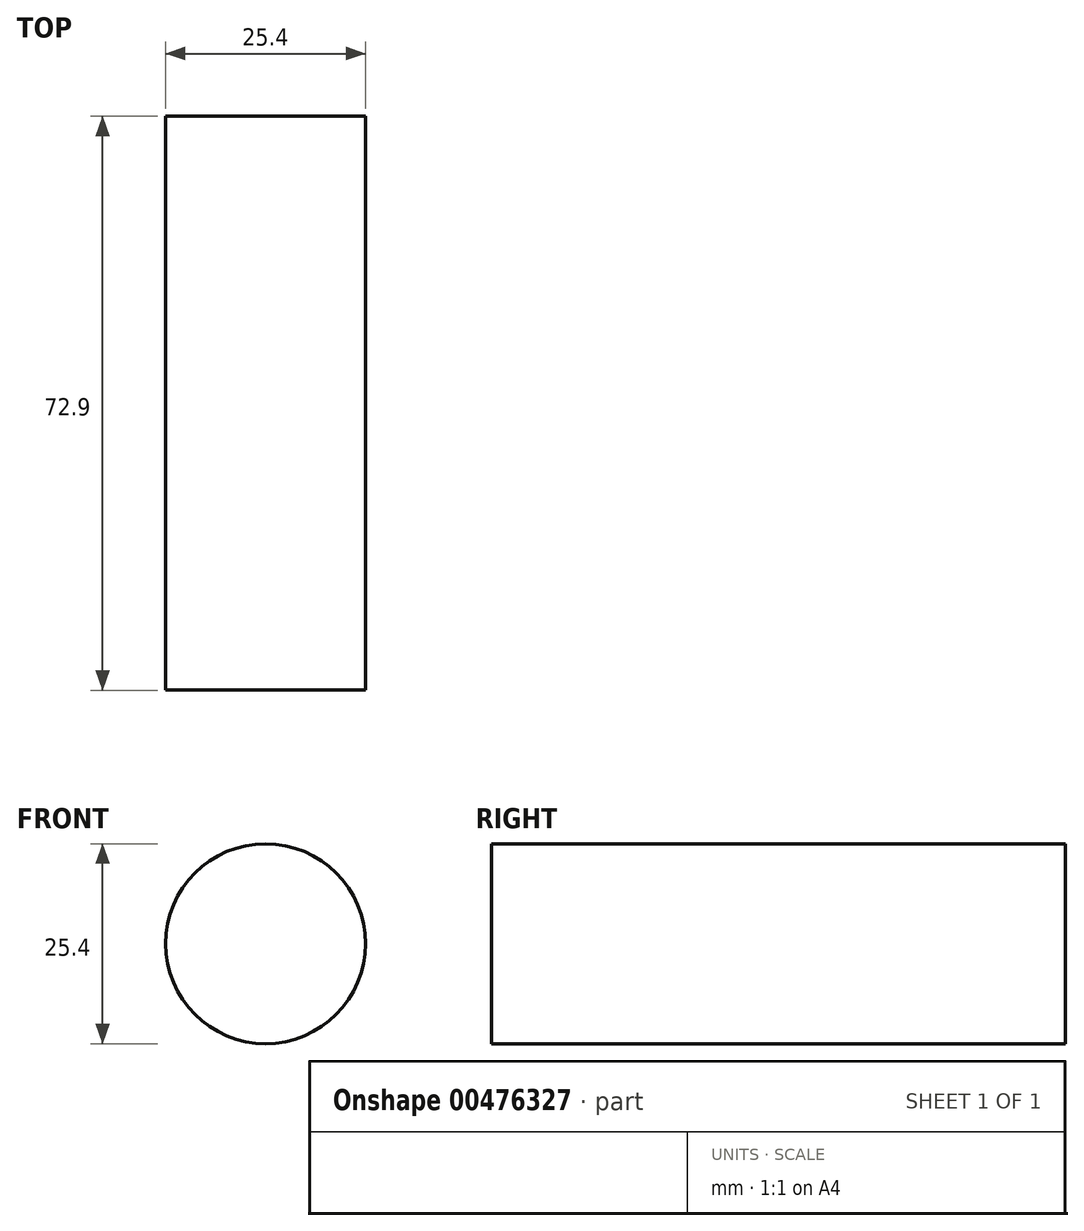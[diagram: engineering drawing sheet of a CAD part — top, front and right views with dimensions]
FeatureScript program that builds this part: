
annotation { "Feature Type Name" : "Feature", "Feature Type Description" : "" }
export const myFeature = defineFeature(function(context is Context, id is Id, definition is map)
    precondition{}
    {
        {
            var Q0;
            Q0=qCreatedBy(makeId("Front.planeOp"),FACE);
            var sketch = newSketch(context, id + "F0", { "sketchPlane" : qUnion([Q0])});
            skCircle(sketch, "E0", {"center": v(0, 0) * mm, "radius": 12.7 * mm});
            skSolve(sketch);
        }
        {
            var Q0;
            Q0 = qSketchRegion(id + "F0", true);
            extrude(context, id + "F1", {"entities" : qUnion([Q0]), "depth" : 72.9 * mm});
        }
        {
            var Q0;
            Q0=qCreatedBy(makeId("Right.planeOp"),FACE);
            var sketch = newSketch(context, id + "F2", { "sketchPlane" : qUnion([Q0])});
            skLineSegment(sketch, "E1", {"start": v(0, 12.7) * mm, "end": v(0, 44.6) * mm});
            skLineSegment(sketch, "E2", {"start": v(0, 44.6) * mm, "end": v(-1.19, 44.6) * mm});
            skLineSegment(sketch, "E3", {"start": v(-1.19, 44.6) * mm, "end": v(-1.19, 12.7) * mm});
            skLineSegment(sketch, "E4.MirrorCS", {"start": v(-71.6, 44.6) * mm, "end": v(-71.6, 12.7) * mm});
            skLineSegment(sketch, "E5.MirrorCS", {"start": v(-72.79, 12.7) * mm, "end": v(-72.79, 44.6) * mm});
            skLineSegment(sketch, "E6.MirrorCS", {"start": v(-72.79, 44.6) * mm, "end": v(-71.6, 44.6) * mm});
            skPoint(sketch, "E7.orphan", {"position": v(0, 12.81) * mm});
            skSolve(sketch);
        }
        {
            var Q0;
            Q0=sQuery(id+"F2.wireOp",EDGE,"E5.MirrorCS");
            var Q1;
            Q1=sQuery(id+"F2.wireOp",EDGE,"E4.MirrorCS");
            var Q2;
            Q2=sQuery(id+"F2.wireOp",EDGE,"E6.MirrorCS");
            var Q3;
            Q3=sQuery(id+"F2.wireOp",EDGE,"E2");
            var Q4;
            Q4=sQuery(id+"F2.wireOp",EDGE,"E1");
            var Q5;
            Q5=makeQuery(id+"F1.opExtrude","SWEPT_FACE",FACE,{"disambiguationData":[OSD([sQuery(id+"F0.wireOp",EDGE,"E0")])]});
            revolve(context, id + "F3", {"bodyType" : ToolBodyType.SURFACE, "operationType" : NewBodyOperationType.ADD, "surfaceEntities" : qUnion([Q0, Q1, Q2, Q3, Q4]), "axis" : qUnion([Q5]), "revolveType" : RevolveType.FULL});
        }
        {
            var Q0;
            Q0=makeQuery(id+"F3.opRevolve","SWEPT_FACE",FACE,{"disambiguationData":[OSD([sQuery(id+"F2.wireOp",EDGE,"E1")])]});
            var sketch = newSketch(context, id + "F4", { "sketchPlane" : qUnion([Q0])});
            skCircle(sketch, "E8", {"center": v(0, -25.88) * mm, "radius": 7.62 * mm});
            skSolve(sketch);
        }
        {
            var Q0;
            Q0=makeQuery(id+"F4.imprint","IMPRINT",FACE,{"disambiguationData":[TD([[makeQuery(id+"F4.imprint","IMPRINT",EDGE,{"derivedFrom":sQuery(id+"F4.wireOp",EDGE,"E8")}),1.0]])]});
            extrude(context, id + "F5", {"entities" : qUnion([Q0]), "operationType" : NewBodyOperationType.REMOVE, "oppositeDirection" : true, "depth" : 127 * mm});
        }
    });
